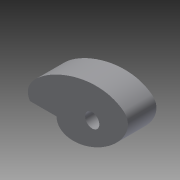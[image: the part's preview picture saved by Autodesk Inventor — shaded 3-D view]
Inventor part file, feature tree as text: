
AUTODESK INVENTOR PART (.ipt)
format: ipt  version: 2014 (Build 180170000, 170)  size: 95,232 bytes
history: native  units: in
note: dims shown in document units (in); Inventor stores cm internally (conversion verified against a paired STEP export)
features: extrude x1, sketch x1
ambient origin geometry x8: Origin, YZ Plane, XZ Plane, XY Plane, X Axis, Y Axis, Z Axis, Center Point
bodies: Solid1 (feature_tree)
feature tree (2):
  extrude  "Extrusion1"  Depth=1.4852in
  sketch  "Sketch1"  dims[d0=2.241in d2=1.4852in d3=2.6061in d4=0.5677in d5=0.4319in d6=1.3501in d7=1.396in d9=0.7824in d10=1.7203in d13=0.727in d14=0.5in d15=1.0in d16=0.0in]
